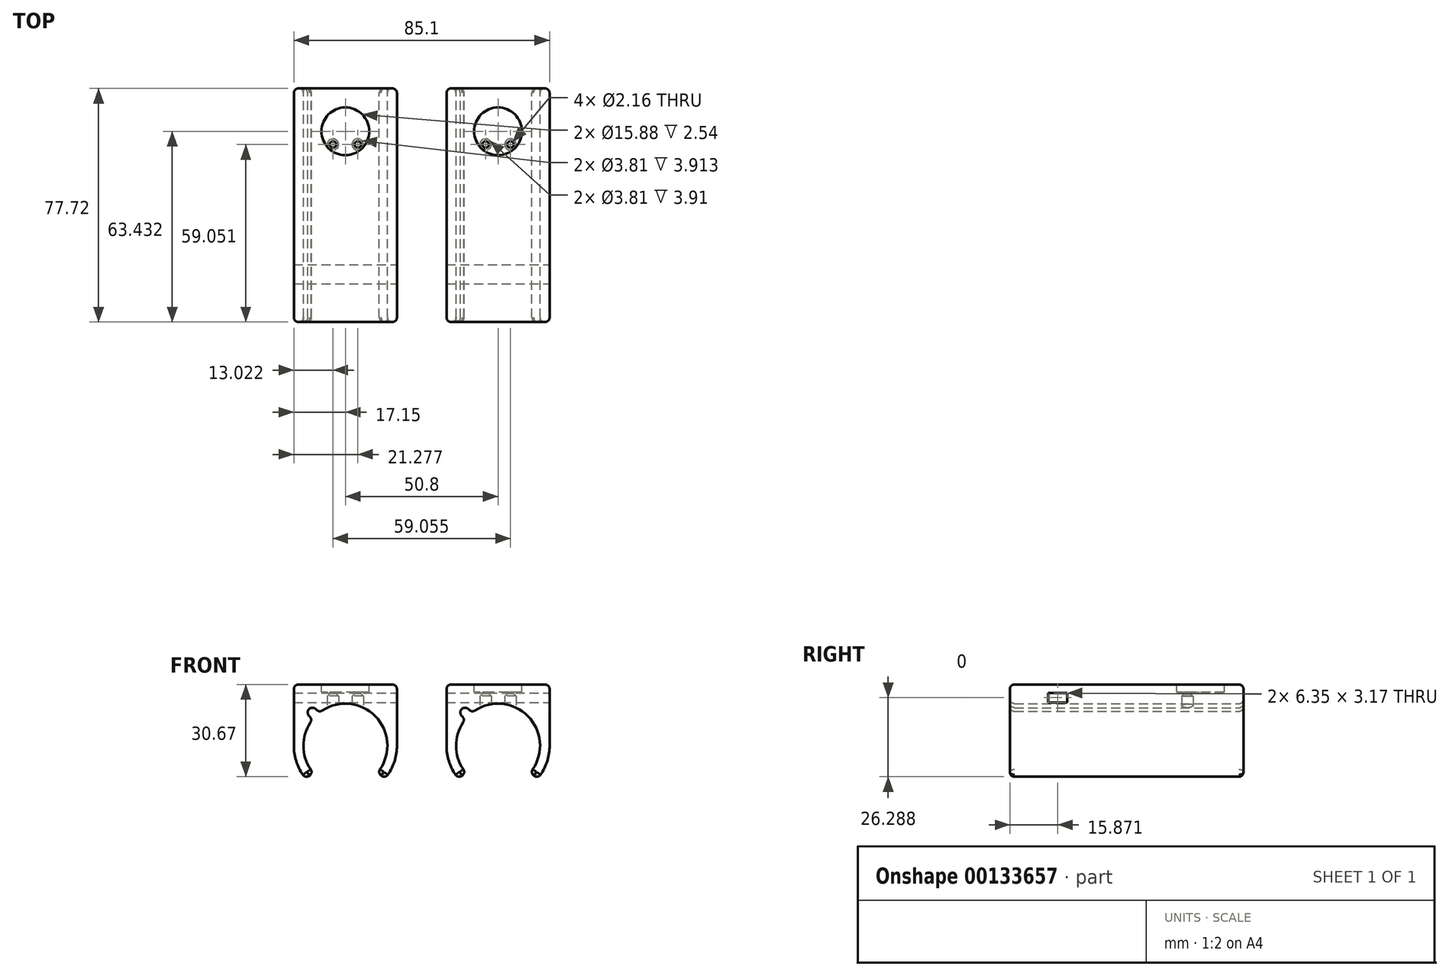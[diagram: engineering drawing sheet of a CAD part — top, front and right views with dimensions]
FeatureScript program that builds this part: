
annotation { "Feature Type Name" : "Feature", "Feature Type Description" : "" }
export const myFeature = defineFeature(function(context is Context, id is Id, definition is map)
    precondition{}
    {
        {
            var Q0;
            Q0=qCreatedBy(makeId("Front.planeOp"),FACE);
            var sketch = newSketch(context, id + "F0", { "sketchPlane" : qUnion([Q0])});
            skArc(sketch, "E0", {"start": v(10.7, -8.98) * mm, "mid": v(10.02, 9.73) * mm, "end": v(-8.66, 10.96) * mm});
            skArc(sketch, "E1.0", {"start": v(-17.15, 0) * mm, "mid": v(-16.11, -5.86) * mm, "end": v(-13.13, -11.02) * mm});
            skLineSegment(sketch, "E2.bottom", {"start": v(-17.15, 20.32) * mm, "end": v(17.14, 20.32) * mm});
            skLineSegment(sketch, "E2.left", {"start": v(-17.15, 20.32) * mm, "end": v(-17.15, 0) * mm});
            skLineSegment(sketch, "E2.right", {"start": v(17.15, 20.32) * mm, "end": v(17.15, 0) * mm});
            skArc(sketch, "E3.trimOffspring", {"start": v(13.13, -11.02) * mm, "mid": v(16.11, -5.86) * mm, "end": v(17.14, 0) * mm});
            skLineSegment(sketch, "E4", {"start": v(-13.13, -11.02) * mm, "end": v(-10.7, -8.98) * mm});
            skLineSegment(sketch, "E5", {"start": v(13.13, -11.02) * mm, "end": v(10.7, -8.98) * mm});
            skArc(sketch, "E6", {"start": v(-9.85, 12.15) * mm, "mid": v(-12.08, 12.17) * mm, "end": v(-12.12, 9.94) * mm});
            skLineSegment(sketch, "E7", {"start": v(-12.12, 9.94) * mm, "end": v(-10.94, 8.69) * mm});
            skLineSegment(sketch, "E8", {"start": v(-9.85, 12.15) * mm, "end": v(-8.66, 10.96) * mm});
            skArc(sketch, "E9.trimOffspring", {"start": v(-10.94, 8.69) * mm, "mid": v(-13.97, -0.19) * mm, "end": v(-10.7, -8.98) * mm});
            skLineSegment(sketch, "E10", {"start": v(0, 0) * mm, "end": v(-10.7, -8.98) * mm, "construction": true});
            skLineSegment(sketch, "E11", {"start": v(0, 0) * mm, "end": v(10.7, -8.98) * mm, "construction": true});
            skSolve(sketch);
        }
        {
            var Q0;
            Q0=makeQuery(id+"F0.imprint","IMPRINT",FACE,{"disambiguationData":[TD([[makeQuery(id+"F0.imprint","IMPRINT",EDGE,{"derivedFrom":sQuery(id+"F0.wireOp",EDGE,"E0")}),-1.0]])]});
            extrude(context, id + "F1", {"entities" : qUnion([Q0]), "depth" : 77.72 * mm});
        }
        {
            var Q0;
            Q0=makeQuery(id+"F1.opExtrude","SWEPT_FACE",FACE,{"disambiguationData":[OSD([sQuery(id+"F0.wireOp",EDGE,"E4")])]});
            var Q1;
            Q1=makeQuery(id+"F1.opExtrude","SWEPT_FACE",FACE,{"disambiguationData":[OSD([sQuery(id+"F0.wireOp",EDGE,"E5")])]});
            fillet(context, id + "F2", {"entities" : qUnion([Q0, Q1]), "radius" : 1.52 * mm, "tangentPropagation" : true, "allowEdgeOverflow" : false});
        }
        {
            var Q0;
            Q0=makeQuery(id+"F1.opExtrude","SWEPT_FACE",FACE,{"disambiguationData":[OSD([sQuery(id+"F0.wireOp",EDGE,"E2.bottom")])]});
            var sketch = newSketch(context, id + "F3", { "sketchPlane" : qUnion([Q0])});
            skCircle(sketch, "E12", {"center": v(0, -14.29) * mm, "radius": 7.94 * mm});
            skSolve(sketch);
        }
        {
            var Q0;
            Q0 = qSketchRegion(id + "F3", true);
            extrude(context, id + "F4", {"entities" : qUnion([Q0]), "operationType" : NewBodyOperationType.REMOVE, "oppositeDirection" : true, "depth" : 2.54 * mm});
        }
        {
            var Q0;
            Q0=makeQuery(id+"F4.boolean.opBoolean","COPY",FACE,{"derivedFrom":makeQuery(id+"F4.opExtrude","CAP_FACE",FACE,{"disambiguationData":[OSD([sQuery(id+"F3.wireOp",EDGE,"E12")])],"isStart":false})});
            var sketch = newSketch(context, id + "F5", { "sketchPlane" : qUnion([Q0])});
            skCircle(sketch, "E13", {"center": v(4.13, -18.67) * mm, "radius": 1.08 * mm});
            skCircle(sketch, "E14", {"center": v(-4.13, -18.67) * mm, "radius": 1.08 * mm});
            skLineSegment(sketch, "E15", {"start": v(-4.13, -18.67) * mm, "end": v(4.13, -18.67) * mm, "construction": true});
            skSolve(sketch);
        }
        {
            var Q0;
            Q0 = qSketchRegion(id + "F5", true);
            extrude(context, id + "F6", {"entities" : qUnion([Q0]), "operationType" : NewBodyOperationType.REMOVE, "endBound" : BoundingType.THROUGH_ALL, "oppositeDirection" : true, "depth" : 25.4 * mm});
        }
        {
            var Q0;
            Q0=makeQuery(id+"F1.opExtrude","SWEPT_FACE",FACE,{"disambiguationData":[OSD([sQuery(id+"F0.wireOp",EDGE,"E2.right")])]});
            var sketch = newSketch(context, id + "F7", { "sketchPlane" : qUnion([Q0])});
            skLineSegment(sketch, "E16.bottom", {"start": v(-65.02, 17.53) * mm, "end": v(-58.67, 17.53) * mm});
            skLineSegment(sketch, "E16.top", {"start": v(-65.02, 14.35) * mm, "end": v(-58.67, 14.35) * mm});
            skLineSegment(sketch, "E16.left", {"start": v(-65.02, 17.53) * mm, "end": v(-65.02, 14.35) * mm});
            skLineSegment(sketch, "E16.right", {"start": v(-58.67, 17.53) * mm, "end": v(-58.67, 14.35) * mm});
            skSolve(sketch);
        }
        {
            var Q0;
            Q0 = qSketchRegion(id + "F7", true);
            extrude(context, id + "F8", {"entities" : qUnion([Q0]), "operationType" : NewBodyOperationType.REMOVE, "endBound" : BoundingType.THROUGH_ALL, "oppositeDirection" : true, "depth" : 15.24 * mm});
        }
        {
            var Q0;
            Q0=makeQuery(id+"F1.opExtrude","SWEPT_EDGE",EDGE,{"disambiguationData":[OSD([sQuery(id+"F0.wireOp",EDGE,"E0"),sQuery(id+"F0.wireOp",EDGE,"E8")])]});
            var Q1;
            Q1=makeQuery(id+"F1.opExtrude","SWEPT_EDGE",EDGE,{"disambiguationData":[OSD([sQuery(id+"F0.wireOp",EDGE,"E7"),sQuery(id+"F0.wireOp",EDGE,"E9.trimOffspring")])]});
            fillet(context, id + "F9", {"entities" : qUnion([Q0, Q1]), "radius" : 1.52 * mm, "tangentPropagation" : true, "allowEdgeOverflow" : false});
        }
        {
            var Q0;
            Q0=makeQuery(id+"F1.opExtrude","CAP_FACE",FACE,{"disambiguationData":[OSD([sQuery(id+"F0.wireOp",EDGE,"E0"),sQuery(id+"F0.wireOp",EDGE,"E1.0"),sQuery(id+"F0.wireOp",EDGE,"E2.bottom"),sQuery(id+"F0.wireOp",EDGE,"E2.left"),sQuery(id+"F0.wireOp",EDGE,"E2.right"),sQuery(id+"F0.wireOp",EDGE,"E3.trimOffspring"),sQuery(id+"F0.wireOp",EDGE,"E4"),sQuery(id+"F0.wireOp",EDGE,"E5"),sQuery(id+"F0.wireOp",EDGE,"E6"),sQuery(id+"F0.wireOp",EDGE,"E7"),sQuery(id+"F0.wireOp",EDGE,"E8"),sQuery(id+"F0.wireOp",EDGE,"E9.trimOffspring")])],"isStart":false});
            var Q1;
            Q1=makeQuery(id+"F1.opExtrude","CAP_FACE",FACE,{"disambiguationData":[OSD([sQuery(id+"F0.wireOp",EDGE,"E0"),sQuery(id+"F0.wireOp",EDGE,"E1.0"),sQuery(id+"F0.wireOp",EDGE,"E2.bottom"),sQuery(id+"F0.wireOp",EDGE,"E2.left"),sQuery(id+"F0.wireOp",EDGE,"E2.right"),sQuery(id+"F0.wireOp",EDGE,"E3.trimOffspring"),sQuery(id+"F0.wireOp",EDGE,"E4"),sQuery(id+"F0.wireOp",EDGE,"E5"),sQuery(id+"F0.wireOp",EDGE,"E6"),sQuery(id+"F0.wireOp",EDGE,"E7"),sQuery(id+"F0.wireOp",EDGE,"E8"),sQuery(id+"F0.wireOp",EDGE,"E9.trimOffspring")])],"isStart":true});
            var Q2;
            Q2=makeQuery(id+"F1.opExtrude","SWEPT_EDGE",EDGE,{"disambiguationData":[OSD([sQuery(id+"F0.wireOp",EDGE,"E2.bottom"),sQuery(id+"F0.wireOp",EDGE,"E2.left")])]});
            var Q3;
            Q3=makeQuery(id+"F1.opExtrude","SWEPT_EDGE",EDGE,{"disambiguationData":[OSD([sQuery(id+"F0.wireOp",EDGE,"E2.bottom"),sQuery(id+"F0.wireOp",EDGE,"E2.right")])]});
            fillet(context, id + "F10", {"entities" : qUnion([Q0, Q1, Q2, Q3]), "radius" : 1.52 * mm, "tangentPropagation" : true, "allowEdgeOverflow" : false});
        }
        {
            var Q0;
            Q0=qCreatedBy(makeId("Top.planeOp"),FACE);
            var sketch = newSketch(context, id + "F11", { "sketchPlane" : qUnion([Q0])});
            skCircle(sketch, "E17", {"center": v(-4.13, -18.67) * mm, "radius": 1.9 * mm});
            skCircle(sketch, "E18", {"center": v(4.13, -18.67) * mm, "radius": 1.9 * mm});
            skLineSegment(sketch, "E19", {"start": v(-4.13, -18.67) * mm, "end": v(4.13, -18.67) * mm, "construction": true});
            skSolve(sketch);
        }
        {
            var Q0;
            Q0 = qSketchRegion(id + "F11", true);
            extrude(context, id + "F12", {"entities" : qUnion([Q0]), "operationType" : NewBodyOperationType.REMOVE, "depth" : 16.5 * mm});
        }
        {
            var Q0;
            Q0=makeQuery(id+"F12.boolean.opBoolean","INTERSECT",EDGE,{"derivedFrom":[makeQuery(id+"F6.boolean.opBoolean","COPY",FACE,{"derivedFrom":makeQuery(id+"F6.opExtrude","SWEPT_FACE",FACE,{"disambiguationData":[OSD([sQuery(id+"F5.wireOp",EDGE,"E14")])]})}),makeQuery(id+"F12.opExtrude","CAP_FACE",FACE,{"disambiguationData":[OSD([sQuery(id+"F11.wireOp",EDGE,"E17")])],"isStart":false})]});
            var Q1;
            Q1=makeQuery(id+"F12.boolean.opBoolean","INTERSECT",EDGE,{"derivedFrom":[makeQuery(id+"F6.boolean.opBoolean","COPY",FACE,{"derivedFrom":makeQuery(id+"F6.opExtrude","SWEPT_FACE",FACE,{"disambiguationData":[OSD([sQuery(id+"F5.wireOp",EDGE,"E13")])]})}),makeQuery(id+"F12.opExtrude","CAP_FACE",FACE,{"disambiguationData":[OSD([sQuery(id+"F11.wireOp",EDGE,"E18")])],"isStart":false})]});
            chamfer(context, id + "F13", {"entities" : qUnion([Q0, Q1]), "width" : 0.76 * mm, "tangentPropagation" : true});
        }
        {
            var Q0;
            Q0=makeQuery(id+"F1.opExtrude","SWEPT_BODY",BODY,{"disambiguationData":[OSD([sQuery(id+"F0.wireOp",EDGE,"E0"),sQuery(id+"F0.wireOp",EDGE,"E1.0"),sQuery(id+"F0.wireOp",EDGE,"E2.bottom"),sQuery(id+"F0.wireOp",EDGE,"E2.left"),sQuery(id+"F0.wireOp",EDGE,"E2.right"),sQuery(id+"F0.wireOp",EDGE,"E3.trimOffspring"),sQuery(id+"F0.wireOp",EDGE,"E4"),sQuery(id+"F0.wireOp",EDGE,"E5"),sQuery(id+"F0.wireOp",EDGE,"E6"),sQuery(id+"F0.wireOp",EDGE,"E7"),sQuery(id+"F0.wireOp",EDGE,"E8"),sQuery(id+"F0.wireOp",EDGE,"E9.trimOffspring")])]});
            transform(context, id + "F14", {"entities" : qUnion([Q0]), "transformType" : TransformType.TRANSLATION_3D, "dx" : 0 * mm, "dy" : 0 * mm, "dz" : 0 * mm, "makeCopy" : true});
        }
        {
            var Q0;
            Q0=makeQuery(id+"F1.opExtrude","SWEPT_BODY",BODY,{"disambiguationData":[OSD([sQuery(id+"F0.wireOp",EDGE,"E0"),sQuery(id+"F0.wireOp",EDGE,"E1.0"),sQuery(id+"F0.wireOp",EDGE,"E2.bottom"),sQuery(id+"F0.wireOp",EDGE,"E2.left"),sQuery(id+"F0.wireOp",EDGE,"E2.right"),sQuery(id+"F0.wireOp",EDGE,"E3.trimOffspring"),sQuery(id+"F0.wireOp",EDGE,"E4"),sQuery(id+"F0.wireOp",EDGE,"E5"),sQuery(id+"F0.wireOp",EDGE,"E6"),sQuery(id+"F0.wireOp",EDGE,"E7"),sQuery(id+"F0.wireOp",EDGE,"E8"),sQuery(id+"F0.wireOp",EDGE,"E9.trimOffspring")])]});
            deleteBodies(context, id + "F15", {"entities" : qUnion([Q0])});
        }
        {
            var Q0;
            Q0=makeQuery(id+"F14.opPattern","COPY",BODY,{"derivedFrom":makeQuery(id+"F1.opExtrude","SWEPT_BODY",BODY,{"disambiguationData":[OSD([sQuery(id+"F0.wireOp",EDGE,"E0"),sQuery(id+"F0.wireOp",EDGE,"E1.0"),sQuery(id+"F0.wireOp",EDGE,"E2.bottom"),sQuery(id+"F0.wireOp",EDGE,"E2.left"),sQuery(id+"F0.wireOp",EDGE,"E2.right"),sQuery(id+"F0.wireOp",EDGE,"E3.trimOffspring"),sQuery(id+"F0.wireOp",EDGE,"E4"),sQuery(id+"F0.wireOp",EDGE,"E5"),sQuery(id+"F0.wireOp",EDGE,"E6"),sQuery(id+"F0.wireOp",EDGE,"E7"),sQuery(id+"F0.wireOp",EDGE,"E8"),sQuery(id+"F0.wireOp",EDGE,"E9.trimOffspring")])]}),"instanceName":"1"});
            transform(context, id + "F16", {"entities" : qUnion([Q0]), "transformType" : TransformType.TRANSLATION_3D, "dx" : 50.8 * mm, "dy" : 0 * mm, "dz" : 0 * mm, "makeCopy" : true});
        }
    });
